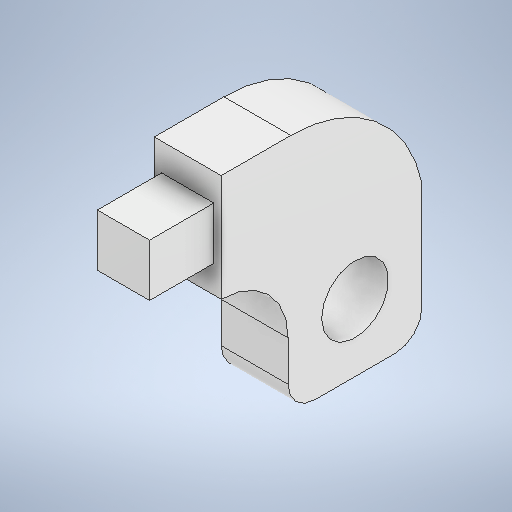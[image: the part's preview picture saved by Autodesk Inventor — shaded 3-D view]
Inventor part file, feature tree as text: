
AUTODESK INVENTOR PART (.ipt)
format: ipt  version: 2025.2 (Build 292293000, 293)  size: 288,256 bytes
history: native  units: mm
features: other x4, extrude x1, sketch x1
ambient origin geometry x8: Origin, YZ Plane, XZ Plane, XY Plane, X Axis, Y Axis, Z Axis, Center Point
bodies: Body1 (feature_tree)
feature tree (6):
  other  "Orgulho_SESI.ipt"
  extrude  "Extrusão1"  Depth=10.0mm TaperAngle=0.0deg
  other  "Apoio::Orgulho_SESI.ipt"
  other  "OperaçãoIdentificador1"
  sketch  "Esboço1"  dims[d0=10.0mm d1=80.0mm d2=0.0mm]
  other  "Apoio"
